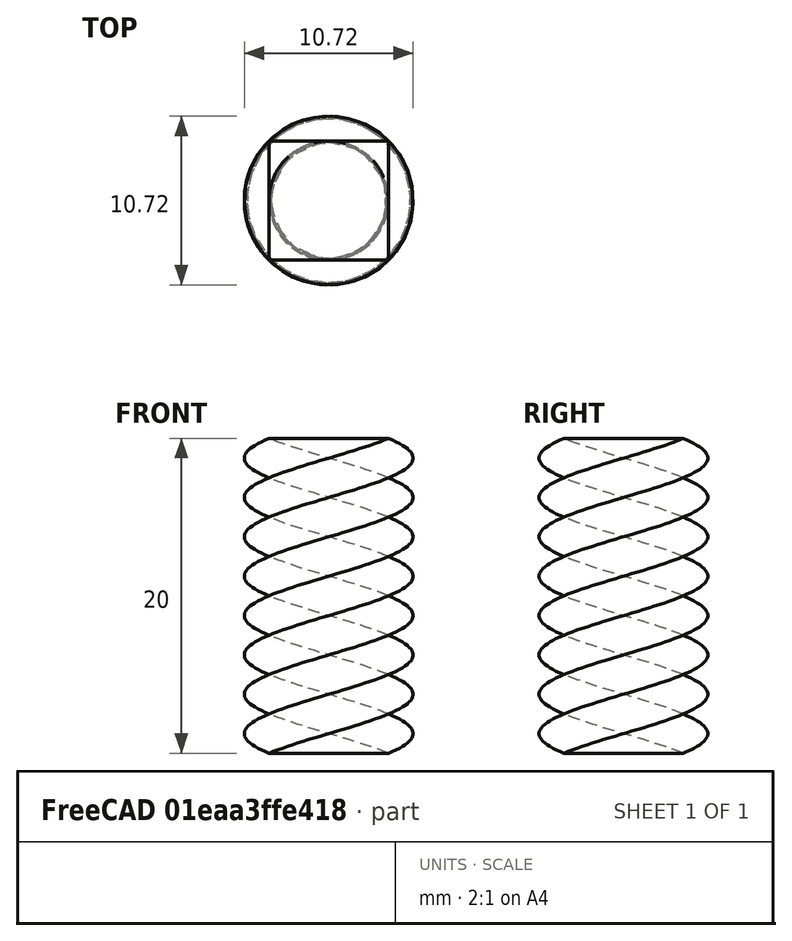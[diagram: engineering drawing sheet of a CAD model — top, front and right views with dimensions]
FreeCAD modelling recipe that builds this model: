
FCSTD DOCUMENT  (FreeCAD 1.0R38806 (Git))
Label: Tuerca
License: All rights reserved
LicenseURL: http://en.wikipedia.org/wiki/All_rights_reserved
objects: Part::Helix×1, Sketcher::SketchObject×1, PartDesign::Body×1, Part::Sweep×1
note: 5 computed .brp shape members not serialized (recipe doc carries the construction recipe); baked Part::Feature solids carry a one-line shape summary decoded from their .brp

FEATURE [Part::Helix] Helix001  label="Hélice001"
  Angle = 0
  AttacherType = Attacher::AttachEngine3D
  Height = 20
  Length = 84.0943
  LocalCoord = 0
  Pitch = 10
  Radius = 6.5
  SegmentLength = 0
  Style = 1
FEATURE [Sketcher::SketchObject] Sketch
  ArcFitTolerance = 1e-06
  AttachmentSupport = -> [XY_Plane]
  FullyConstrained = false
  MakeInternals = false
  MapMode = 5
  sketch-geometry (4):
    g0: LineSegment StartX=-3.79223 StartY=3.79223 StartZ=0 EndX=-3.79223 EndY=-3.79223 EndZ=0
    g1: LineSegment StartX=-3.79223 StartY=-3.79223 StartZ=0 EndX=3.79223 EndY=-3.79223 EndZ=0
    g2: LineSegment StartX=3.79223 StartY=-3.79223 StartZ=0 EndX=3.79223 EndY=3.79223 EndZ=0
    g3: LineSegment StartX=3.79223 StartY=3.79223 StartZ=0 EndX=-3.79223 EndY=3.79223 EndZ=0
  constraints (9):
    c: Coincident(g0,g1)
    c: Coincident(g1,g2)
    c: Coincident(g2,g3)
    c: Coincident(g3,g0)
    c: Vertical(g2)
    c: Horizontal(g1)
    c: Symmetric(g0,g0,g-1)
    c: Symmetric(g0,g2,g-2)
    c: Equal(g3,g0)
FEATURE [PartDesign::Body] Body
  AllowCompound = false
  Group = -> [Sketch]
  Origin = -> Origin
FEATURE [Part::Sweep] Sweep
  Frenet = true
  Sections = -> [Sketch]
  Solid = true
  Spine = -> Helix001 [Edge1]
  Transition = 1
